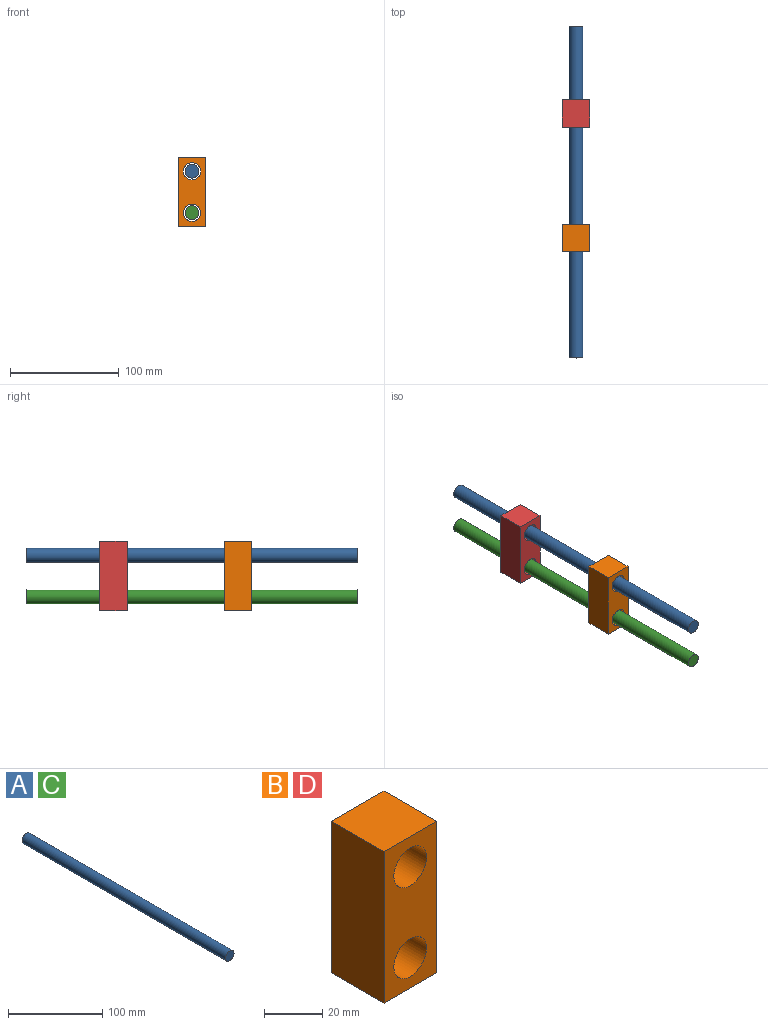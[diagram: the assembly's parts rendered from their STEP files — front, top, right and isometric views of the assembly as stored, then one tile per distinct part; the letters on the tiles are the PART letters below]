
ASSEMBLY  parts=4 mates=3
PART A: 3 faces, bbox 12.7x304.8x12.7 mm
  f0: cylinder r=6.35mm len=304.8mm, axis (0,1,0), area 12161mm2, adj f1,f2
  f1: plane 12.7x12.7mm, normal (0,-1,0), area 126.7mm2, adj f0
  f2: plane 12.7x12.7mm, normal (0,1,0), area 126.7mm2, adj f0
PART B: 8 faces, bbox 25.4x25.4x63.5 mm
  f0: plane 25.4x25.4mm, normal (0,0,1), area 645.2mm2, adj f1,f5,f6,f7
  f1: plane 63.5x25.4mm, normal (-1,0,0), area 1612.9mm2, adj f0,f2,f6,f7
  f2: plane 25.4x25.4mm, normal (0,0,-1), area 645.2mm2, adj f1,f5,f6,f7
  f3: cylinder r=7.94mm len=25.4mm, axis (0,1,0), area 1266.8mm2, adj f6,f7
  f4: cylinder r=7.94mm len=25.4mm, axis (0,1,0), area 1266.8mm2, adj f6,f7
  f5: plane 63.5x25.4mm, normal (1,0,0), area 1612.9mm2, adj f0,f2,f6,f7
  f6: plane 63.5x25.4mm, normal (0,-1,0), area 1217mm2, adj f0,f1,f2,f3,f4,f5
  f7: plane 63.5x25.4mm, normal (0,1,0), area 1217mm2, adj f0,f1,f2,f3,f4,f5
PART C: same geometry as A
PART D: same geometry as B
PLACE A t=(0,0,38.1)mm
PLACE B t=(0,-131.07,0)mm
PLACE C at identity
PLACE D t=(0,-16.77,0)mm
MATE fastened C.f0 <-> A.f2  axis (0,1,0) through (0,0,0)mm
MATE fastened B.f3 <-> D.f3  axis (0,1,0) through (0,-181.87,0)mm
MATE slider D.f4 <-> A.f0  axis (0,1,0) through (0,-67.57,38.1)mm
